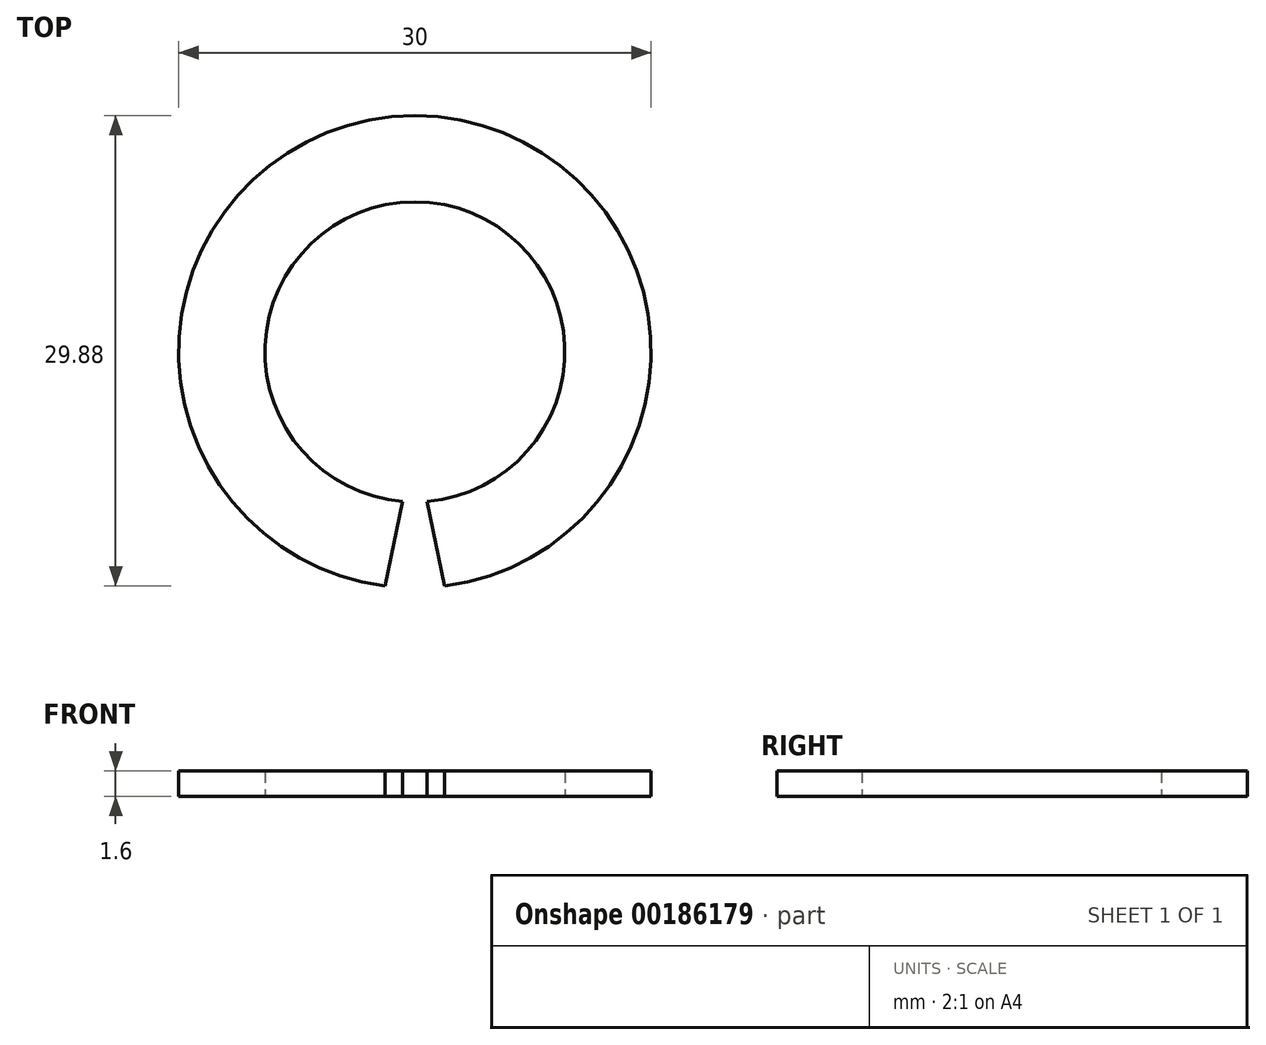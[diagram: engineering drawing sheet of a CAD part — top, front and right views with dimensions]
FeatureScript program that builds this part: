
annotation { "Feature Type Name" : "Feature", "Feature Type Description" : "" }
export const myFeature = defineFeature(function(context is Context, id is Id, definition is map)
    precondition{}
    {
        {
            var Q0;
            Q0=qCreatedBy(makeId("Top.planeOp"),FACE);
            var sketch = newSketch(context, id + "F0", { "sketchPlane" : qUnion([Q0])});
            skArc(sketch, "E0", {"start": v(0.77, -9.5) * mm, "mid": v(0, 9.53) * mm, "end": v(-0.77, -9.5) * mm});
            skArc(sketch, "E1", {"start": v(1.9, -14.88) * mm, "mid": v(0, 15) * mm, "end": v(-1.9, -14.88) * mm});
            skLineSegment(sketch, "E2", {"start": v(-0.77, -9.5) * mm, "end": v(-1.9, -14.88) * mm});
            skLineSegment(sketch, "E3.MirrorCS", {"start": v(0.77, -9.5) * mm, "end": v(1.9, -14.88) * mm});
            skSolve(sketch);
        }
        {
            var Q0;
            Q0 = qSketchRegion(id + "F0", true);
            extrude(context, id + "F1", {"entities" : qUnion([Q0]), "endBound" : BoundingType.SYMMETRIC, "depth" : 1.6 * mm});
        }
    });
